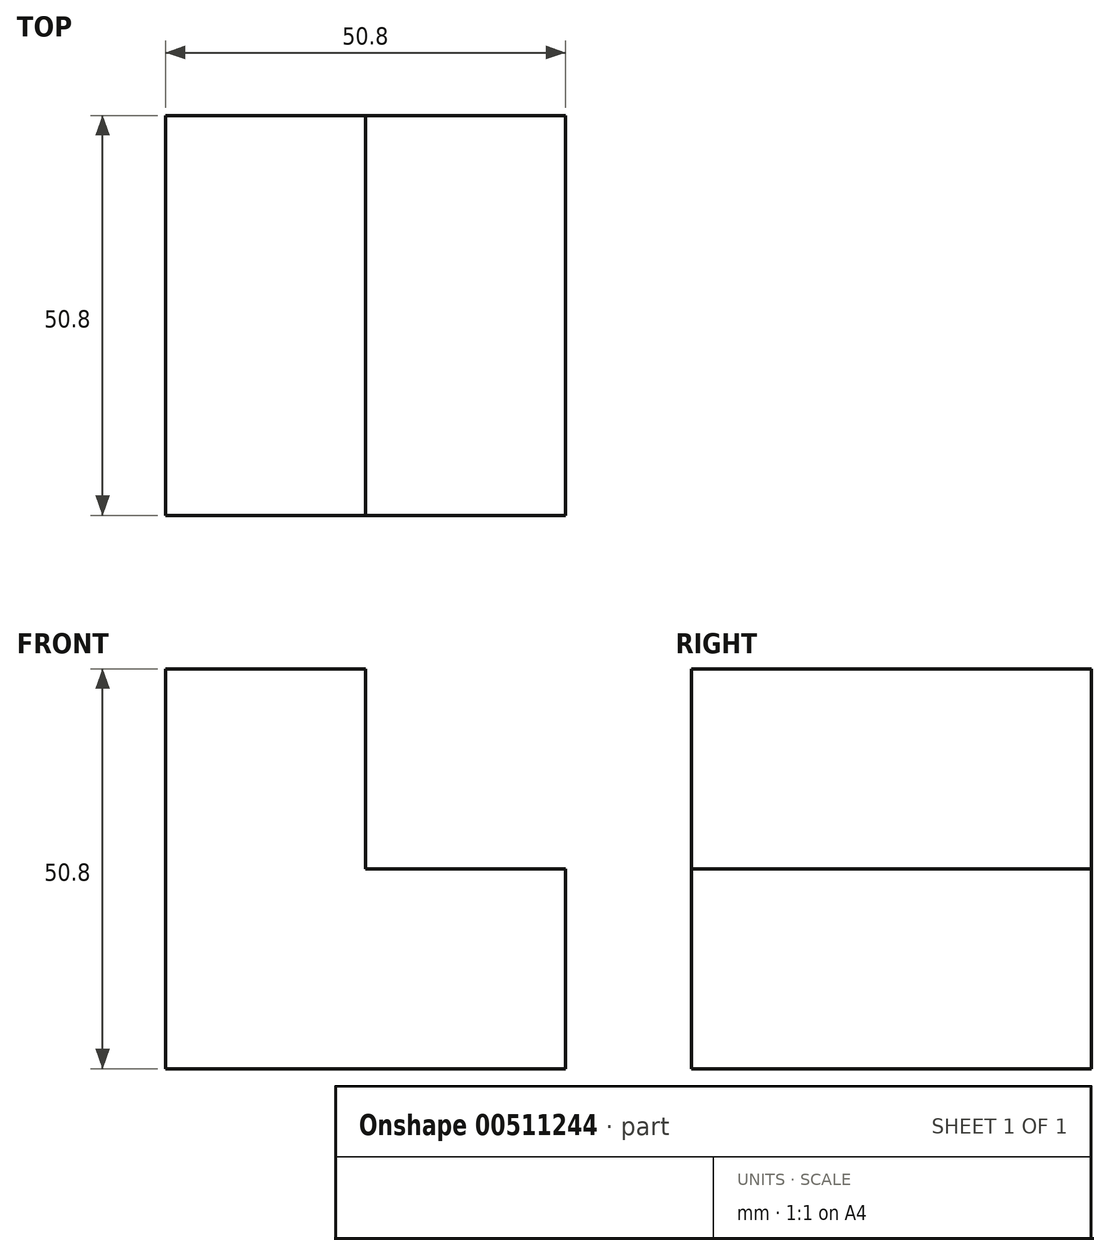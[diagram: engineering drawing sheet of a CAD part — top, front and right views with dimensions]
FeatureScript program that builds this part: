
annotation { "Feature Type Name" : "Feature", "Feature Type Description" : "" }
export const myFeature = defineFeature(function(context is Context, id is Id, definition is map)
    precondition{}
    {
        {
            var Q0;
            Q0=qCreatedBy(makeId("Front.planeOp"),FACE);
            var sketch = newSketch(context, id + "F0", { "sketchPlane" : qUnion([Q0])});
            skLineSegment(sketch, "E0", {"start": v(-50.8, 47.44) * mm, "end": v(-50.8, -3.36) * mm});
            skLineSegment(sketch, "E1", {"start": v(-50.8, 47.44) * mm, "end": v(-25.4, 47.44) * mm});
            skLineSegment(sketch, "E2", {"start": v(-25.4, 47.44) * mm, "end": v(-25.4, 22.04) * mm});
            skLineSegment(sketch, "E3", {"start": v(-25.4, 22.04) * mm, "end": v(0, 22.04) * mm});
            skLineSegment(sketch, "E4", {"start": v(0, 22.04) * mm, "end": v(0, -3.36) * mm});
            skLineSegment(sketch, "E5", {"start": v(-50.8, -3.36) * mm, "end": v(0, -3.36) * mm});
            skSolve(sketch);
        }
        {
            var Q0;
            Q0 = qSketchRegion(id + "F0", true);
            extrude(context, id + "F1", {"entities" : qUnion([Q0]), "depth" : 50.8 * mm});
        }
    });
